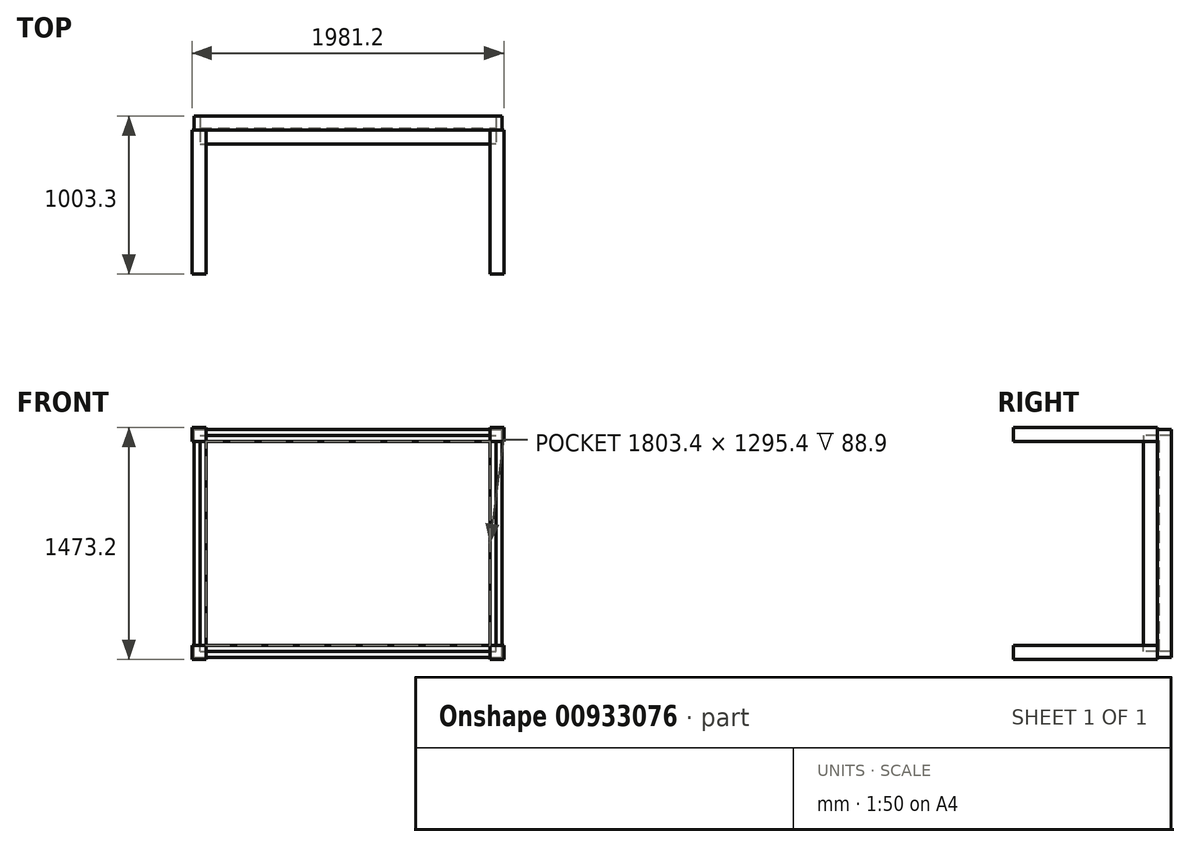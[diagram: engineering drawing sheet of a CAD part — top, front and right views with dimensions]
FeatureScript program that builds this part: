
annotation { "Feature Type Name" : "Feature", "Feature Type Description" : "" }
export const myFeature = defineFeature(function(context is Context, id is Id, definition is map)
    precondition{}
    {
        {
            var Q0;
            Q0=qCreatedBy(makeId("Front.planeOp"),FACE);
            var sketch = newSketch(context, id + "F0", { "sketchPlane" : qUnion([Q0])});
            skLineSegment(sketch, "E0.bottom", {"start": v(44.45, 44.45) * mm, "end": v(-44.45, 44.45) * mm});
            skLineSegment(sketch, "E0.top", {"start": v(44.45, -44.45) * mm, "end": v(-44.45, -44.45) * mm});
            skLineSegment(sketch, "E0.left", {"start": v(44.45, 44.45) * mm, "end": v(44.45, -44.45) * mm});
            skLineSegment(sketch, "E0.right", {"start": v(-44.45, 44.45) * mm, "end": v(-44.45, -44.45) * mm});
            skPoint(sketch, "E0.middle", {"position": v(0, 0) * mm});
            skSolve(sketch);
        }
        {
            var Q0;
            Q0 = qSketchRegion(id + "F0", true);
            extrude(context, id + "F1", {"entities" : qUnion([Q0]), "depth" : 914.4 * mm, "offsetDistance" : 25.4 * mm});
        }
        {
            var Q0;
            Q0=makeQuery(id+"F1.opExtrude","SWEPT_FACE",FACE,{"disambiguationData":[OSD([sQuery(id+"F0.wireOp",EDGE,"E0.left")])]});
            var sketch = newSketch(context, id + "F2", { "sketchPlane" : qUnion([Q0])});
            skLineSegment(sketch, "E1.bottom", {"start": v(0, -6.35) * mm, "end": v(-88.9, -6.35) * mm});
            skLineSegment(sketch, "E1.top", {"start": v(0, -44.45) * mm, "end": v(-88.9, -44.45) * mm});
            skLineSegment(sketch, "E1.left", {"start": v(0, -6.35) * mm, "end": v(0, -44.45) * mm});
            skLineSegment(sketch, "E1.right", {"start": v(-88.9, -6.35) * mm, "end": v(-88.9, -44.45) * mm});
            skSolve(sketch);
        }
        {
            var Q0;
            Q0 = qSketchRegion(id + "F2", true);
            extrude(context, id + "F3", {"entities" : qUnion([Q0]), "operationType" : NewBodyOperationType.ADD, "depth" : 1803.4 * mm, "offsetDistance" : 25.4 * mm});
        }
        {
            var Q0;
            Q0=qCreatedBy(makeId("Front.planeOp"),FACE);
            var sketch = newSketch(context, id + "F4", { "sketchPlane" : qUnion([Q0])});
            skLineSegment(sketch, "E2.bottom", {"start": v(1847.85, 44.45) * mm, "end": v(1936.75, 44.45) * mm});
            skLineSegment(sketch, "E2.top", {"start": v(1847.85, -44.45) * mm, "end": v(1936.75, -44.45) * mm});
            skLineSegment(sketch, "E2.left", {"start": v(1847.85, 44.45) * mm, "end": v(1847.85, -44.45) * mm});
            skLineSegment(sketch, "E2.right", {"start": v(1936.75, 44.45) * mm, "end": v(1936.75, -44.45) * mm});
            skSolve(sketch);
        }
        {
            var Q0;
            Q0=makeQuery(id+"F4.imprint","IMPRINT",FACE,{"disambiguationData":[TD([[makeQuery(id+"F4.imprint","IMPRINT",EDGE,{"derivedFrom":sQuery(id+"F4.wireOp",EDGE,"E2.bottom")}),-1.0]])]});
            extrude(context, id + "F5", {"entities" : qUnion([Q0]), "operationType" : NewBodyOperationType.ADD, "depth" : 914.4 * mm, "offsetDistance" : 25.4 * mm});
        }
        {
            var Q0;
            Q0=makeQuery(id+"F5.opExtrude","SWEPT_FACE",FACE,{"disambiguationData":[OSD([sQuery(id+"F4.wireOp",EDGE,"E2.top")])]});
            var sketch = newSketch(context, id + "F6", { "sketchPlane" : qUnion([Q0])});
            skLineSegment(sketch, "E3.bottom", {"start": v(1885.95, 0) * mm, "end": v(1847.85, 0) * mm});
            skLineSegment(sketch, "E3.top", {"start": v(1885.95, 88.9) * mm, "end": v(1847.85, 88.9) * mm});
            skLineSegment(sketch, "E3.left", {"start": v(1885.95, 0) * mm, "end": v(1885.95, 88.9) * mm});
            skLineSegment(sketch, "E3.right", {"start": v(1847.85, 0) * mm, "end": v(1847.85, 88.9) * mm});
            skSolve(sketch);
        }
        {
            var Q0;
            Q0 = qSketchRegion(id + "F6", true);
            extrude(context, id + "F7", {"entities" : qUnion([Q0]), "operationType" : NewBodyOperationType.ADD, "depth" : 1295.4 * mm, "offsetDistance" : 25.4 * mm});
        }
        {
            var Q0;
            Q0=qCreatedBy(makeId("Front.planeOp"),FACE);
            var sketch = newSketch(context, id + "F8", { "sketchPlane" : qUnion([Q0])});
            skLineSegment(sketch, "E4.bottom", {"start": v(1936.75, -1339.85) * mm, "end": v(1847.85, -1339.85) * mm});
            skLineSegment(sketch, "E4.top", {"start": v(1936.75, -1428.75) * mm, "end": v(1847.85, -1428.75) * mm});
            skLineSegment(sketch, "E4.left", {"start": v(1936.75, -1339.85) * mm, "end": v(1936.75, -1428.75) * mm});
            skLineSegment(sketch, "E4.right", {"start": v(1847.85, -1339.85) * mm, "end": v(1847.85, -1428.75) * mm});
            skSolve(sketch);
        }
        {
            var Q0;
            Q0 = qSketchRegion(id + "F8", true);
            extrude(context, id + "F9", {"entities" : qUnion([Q0]), "operationType" : NewBodyOperationType.ADD, "depth" : 914.4 * mm, "offsetDistance" : 25.4 * mm});
        }
        {
            var Q0;
            Q0=makeQuery(id+"F1.opExtrude","SWEPT_FACE",FACE,{"disambiguationData":[OSD([sQuery(id+"F0.wireOp",EDGE,"E0.top")])]});
            var sketch = newSketch(context, id + "F10", { "sketchPlane" : qUnion([Q0])});
            skLineSegment(sketch, "E5.bottom", {"start": v(6.35, 0) * mm, "end": v(44.45, 0) * mm});
            skLineSegment(sketch, "E5.top", {"start": v(6.35, 88.9) * mm, "end": v(44.45, 88.9) * mm});
            skLineSegment(sketch, "E5.left", {"start": v(6.35, 0) * mm, "end": v(6.35, 88.9) * mm});
            skLineSegment(sketch, "E5.right", {"start": v(44.45, 0) * mm, "end": v(44.45, 88.9) * mm});
            skSolve(sketch);
        }
        {
            var Q0;
            Q0 = qSketchRegion(id + "F10", true);
            extrude(context, id + "F11", {"entities" : qUnion([Q0]), "operationType" : NewBodyOperationType.ADD, "depth" : 1295.4 * mm, "offsetDistance" : 25.4 * mm});
        }
        {
            var Q0;
            Q0=qCreatedBy(makeId("Front.planeOp"),FACE);
            var sketch = newSketch(context, id + "F12", { "sketchPlane" : qUnion([Q0])});
            skLineSegment(sketch, "E6.bottom", {"start": v(-44.45, -1339.85) * mm, "end": v(44.45, -1339.85) * mm});
            skLineSegment(sketch, "E6.top", {"start": v(-44.45, -1428.75) * mm, "end": v(44.45, -1428.75) * mm});
            skLineSegment(sketch, "E6.left", {"start": v(-44.45, -1339.85) * mm, "end": v(-44.45, -1428.75) * mm});
            skLineSegment(sketch, "E6.right", {"start": v(44.45, -1339.85) * mm, "end": v(44.45, -1428.75) * mm});
            skSolve(sketch);
        }
        {
            var Q0;
            Q0 = qSketchRegion(id + "F12", true);
            extrude(context, id + "F13", {"entities" : qUnion([Q0]), "operationType" : NewBodyOperationType.ADD, "depth" : 914.4 * mm, "offsetDistance" : 25.4 * mm});
        }
        {
            var Q0;
            Q0=makeQuery(id+"F13.opExtrude","SWEPT_FACE",FACE,{"disambiguationData":[OSD([sQuery(id+"F12.wireOp",EDGE,"E6.right")])]});
            var sketch = newSketch(context, id + "F14", { "sketchPlane" : qUnion([Q0])});
            skLineSegment(sketch, "E7.bottom", {"start": v(0, -1377.95) * mm, "end": v(-88.9, -1377.95) * mm});
            skLineSegment(sketch, "E7.top", {"start": v(0, -1339.85) * mm, "end": v(-88.9, -1339.85) * mm});
            skLineSegment(sketch, "E7.left", {"start": v(0, -1377.95) * mm, "end": v(0, -1339.85) * mm});
            skLineSegment(sketch, "E7.right", {"start": v(-88.9, -1377.95) * mm, "end": v(-88.9, -1339.85) * mm});
            skSolve(sketch);
        }
        {
            var Q0;
            Q0 = qSketchRegion(id + "F14", true);
            extrude(context, id + "F15", {"entities" : qUnion([Q0]), "operationType" : NewBodyOperationType.ADD, "depth" : 1803.4 * mm, "offsetDistance" : 25.4 * mm});
        }
        {
            var Q0;
            Q0=qCreatedBy(makeId("Front.planeOp"),FACE);
            var sketch = newSketch(context, id + "F16", { "sketchPlane" : qUnion([Q0])});
            skLineSegment(sketch, "E8.bottom", {"start": v(6.35, -1377.95) * mm, "end": v(1885.95, -1377.95) * mm});
            skLineSegment(sketch, "E8.top", {"start": v(6.35, -6.35) * mm, "end": v(1885.95, -6.35) * mm});
            skLineSegment(sketch, "E8.left", {"start": v(6.35, -1377.95) * mm, "end": v(6.35, -6.35) * mm});
            skLineSegment(sketch, "E8.right", {"start": v(1885.95, -1377.95) * mm, "end": v(1885.95, -6.35) * mm});
            skSolve(sketch);
        }
        {
            var Q0;
            Q0 = qSketchRegion(id + "F16", true);
            extrude(context, id + "F17", {"entities" : qUnion([Q0]), "operationType" : NewBodyOperationType.ADD, "oppositeDirection" : true, "depth" : 12.7 * mm, "offsetDistance" : 25.4 * mm});
        }
        {
            var Q0;
            Q0=qCreatedBy(makeId("Front.planeOp"),FACE);
            var sketch = newSketch(context, id + "F18", { "sketchPlane" : qUnion([Q0])});
            skLineSegment(sketch, "E9.bottom", {"start": v(6.35, -6.35) * mm, "end": v(1885.95, -6.35) * mm});
            skLineSegment(sketch, "E9.top", {"start": v(6.35, -1377.95) * mm, "end": v(1885.95, -1377.95) * mm});
            skLineSegment(sketch, "E9.left", {"start": v(6.35, -6.35) * mm, "end": v(6.35, -1377.95) * mm});
            skLineSegment(sketch, "E9.right", {"start": v(1885.95, -6.35) * mm, "end": v(1885.95, -1377.95) * mm});
            skLineSegment(sketch, "E10.bottom", {"start": v(-31.75, -1416.05) * mm, "end": v(1924.05, -1416.05) * mm});
            skLineSegment(sketch, "E10.top", {"start": v(-31.75, 31.75) * mm, "end": v(1924.05, 31.75) * mm});
            skLineSegment(sketch, "E10.left", {"start": v(-31.75, -1416.05) * mm, "end": v(-31.75, 31.75) * mm});
            skLineSegment(sketch, "E10.right", {"start": v(1924.05, -1416.05) * mm, "end": v(1924.05, 31.75) * mm});
            skSolve(sketch);
        }
        {
            var Q0;
            Q0 = qSketchRegion(id + "F18", true);
            extrude(context, id + "F19", {"entities" : qUnion([Q0]), "operationType" : NewBodyOperationType.ADD, "oppositeDirection" : true, "depth" : 88.9 * mm, "offsetDistance" : 25.4 * mm});
        }
    });
